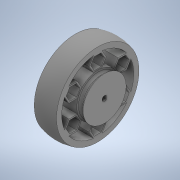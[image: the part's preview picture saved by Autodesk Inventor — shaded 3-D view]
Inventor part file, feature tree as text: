
AUTODESK INVENTOR PART (.ipt)
format: ipt  version: 2020 (Build 240168000, 168)  size: 353,792 bytes
history: native  units: in
note: dims shown in document units (in); Inventor stores cm internally (conversion verified against a paired STEP export)
features: sketch x4, extrude x2, revolve x2, projected_geometry x1
ambient origin geometry x8: Origin, YZ Plane, XZ Plane, XY Plane, X Axis, Y Axis, Z Axis, Center Point
bodies: Solid1 (feature_tree)
feature tree (9):
  extrude  "Extrusion1"  Depth=0.0394in
  sketch  "Sketch3"  dims[d6=0.9843in d7=0.1575in]
  revolve  "Revolution1"  [1 undecoded]
  extrude  "Extrusion2"  Depth=0.1575in
  revolve  "Revolution2"  [1 undecoded]
  sketch  "Sketch1"  dims[d0=0.1181in d1=0.0394in]
  sketch  "Sketch2"  dims[d3=1.8898in d4=0.1181in]
  projected_geometry  "Projected Loop1"
  sketch  "Sketch4"  dims[d8=0.0in d9=1.8898in d10=0.1181in d11=0.0315in d12=2.3622in d14=360.0deg d16=0.5118in d17=0.0in d19=360.0deg d20=0.0787in d22=90.0deg d24=0.0394in d25=90.0deg d26=45.0deg]
note: 2 required parameter values undecoded (feature->parameter linkage not recoverable at this tier; creation-order binding heuristic only, values carry confidence <= 0.55)
